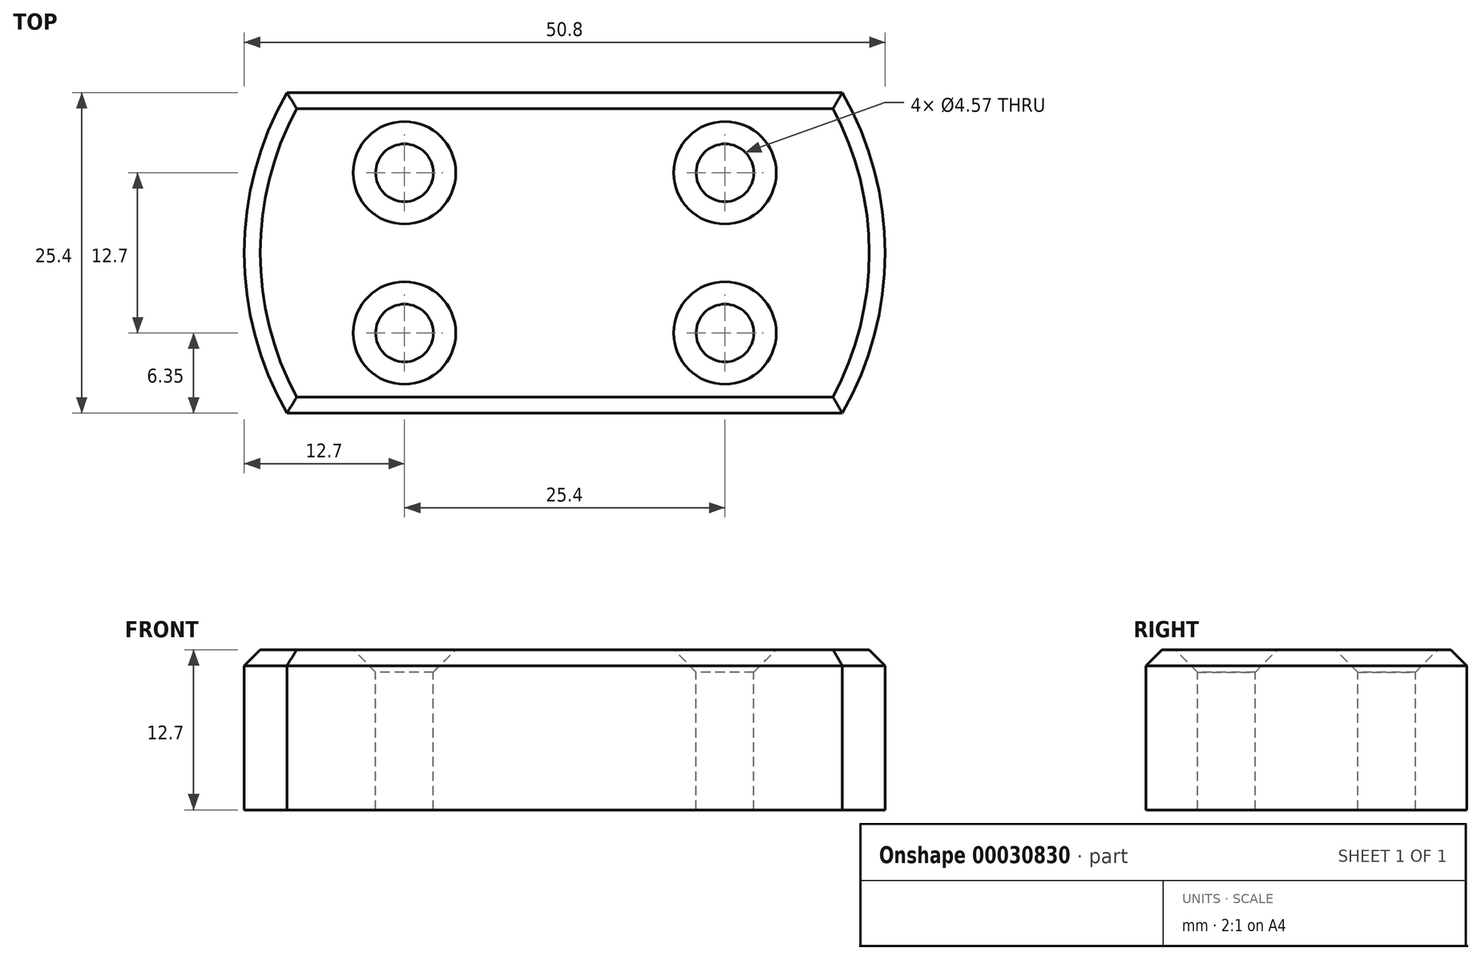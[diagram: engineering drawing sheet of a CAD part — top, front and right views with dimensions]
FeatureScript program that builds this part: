
annotation { "Feature Type Name" : "Feature", "Feature Type Description" : "" }
export const myFeature = defineFeature(function(context is Context, id is Id, definition is map)
    precondition{}
    {
        {
            var Q0;
            Q0=qCreatedBy(makeId("Top.planeOp"),FACE);
            var sketch = newSketch(context, id + "F0", { "sketchPlane" : qUnion([Q0])});
            skArc(sketch, "E0", {"start": v(-22, 12.7) * mm, "mid": v(-25.4, 0) * mm, "end": v(-22, -12.7) * mm});
            skLineSegment(sketch, "E1", {"start": v(-22, 12.7) * mm, "end": v(22, 12.7) * mm});
            skLineSegment(sketch, "E2", {"start": v(-22, -12.7) * mm, "end": v(22, -12.7) * mm});
            skArc(sketch, "E3.trimOffspring", {"start": v(22, -12.7) * mm, "mid": v(25.4, 0) * mm, "end": v(22, 12.7) * mm});
            skSolve(sketch);
        }
        {
            var Q0;
            Q0=makeQuery(id+"F0.imprint","IMPRINT",FACE,{"disambiguationData":[TD([[makeQuery(id+"F0.imprint","IMPRINT",EDGE,{"derivedFrom":sQuery(id+"F0.wireOp",EDGE,"E0")}),1.0]])]});
            extrude(context, id + "F1", {"entities" : qUnion([Q0]), "depth" : 12.7 * mm});
        }
        {
            var Q0;
            Q0=makeQuery(id+"F1.opExtrude","CAP_FACE",FACE,{"disambiguationData":[OSD([sQuery(id+"F0.wireOp",EDGE,"E0"),sQuery(id+"F0.wireOp",EDGE,"E1"),sQuery(id+"F0.wireOp",EDGE,"E2"),sQuery(id+"F0.wireOp",EDGE,"E3.trimOffspring")])],"isStart":false});
            var sketch = newSketch(context, id + "F2", { "sketchPlane" : qUnion([Q0])});
            skPoint(sketch, "E4", {"position": v(-12.7, 6.35) * mm});
            skPoint(sketch, "E5", {"position": v(-12.7, -6.35) * mm});
            skPoint(sketch, "E6", {"position": v(12.7, -6.35) * mm});
            skPoint(sketch, "E7", {"position": v(12.7, 6.35) * mm});
            skSolve(sketch);
        }
        {
            var Q0;
            Q0=sQuery(id+"F2.wireOp",VERTEX,"E4");
            var Q1;
            Q1=sQuery(id+"F2.wireOp",VERTEX,"E5");
            var Q2;
            Q2=sQuery(id+"F2.wireOp",VERTEX,"E6");
            var Q3;
            Q3=sQuery(id+"F2.wireOp",VERTEX,"E7");
            var Q4;
            Q4=makeQuery(id+"F1.opExtrude","SWEPT_BODY",BODY,{"disambiguationData":[OSD([sQuery(id+"F0.wireOp",EDGE,"E0"),sQuery(id+"F0.wireOp",EDGE,"E1"),sQuery(id+"F0.wireOp",EDGE,"E2"),sQuery(id+"F0.wireOp",EDGE,"E3.trimOffspring")])]});
            hole(context, id + "F3", {"style" : HoleStyle.C_SINK, "holeDiameter" : 4.57 * mm, "cSinkDiameter" : 8.13 * mm, "endStyle" : HoleEndStyle.THROUGH, "locations" : qUnion([Q0, Q1, Q2, Q3]), "scope" : qUnion([Q4]), "cSinkAngle" : 90 * degree});
        }
        {
            var Q0;
            Q0=makeQuery(id+"F1.opExtrude","CAP_EDGE",EDGE,{"disambiguationData":[OSD([sQuery(id+"F0.wireOp",EDGE,"E2")])],"isStart":false});
            var Q1;
            Q1=makeQuery(id+"F1.opExtrude","CAP_EDGE",EDGE,{"disambiguationData":[OSD([sQuery(id+"F0.wireOp",EDGE,"E3.trimOffspring")])],"isStart":false});
            var Q2;
            Q2=makeQuery(id+"F1.opExtrude","CAP_EDGE",EDGE,{"disambiguationData":[OSD([sQuery(id+"F0.wireOp",EDGE,"E1")])],"isStart":false});
            var Q3;
            Q3=makeQuery(id+"F1.opExtrude","CAP_EDGE",EDGE,{"disambiguationData":[OSD([sQuery(id+"F0.wireOp",EDGE,"E0")])],"isStart":false});
            chamfer(context, id + "F4", {"entities" : qUnion([Q0, Q1, Q2, Q3]), "width" : 1.27 * mm, "tangentPropagation" : true});
        }
    });
